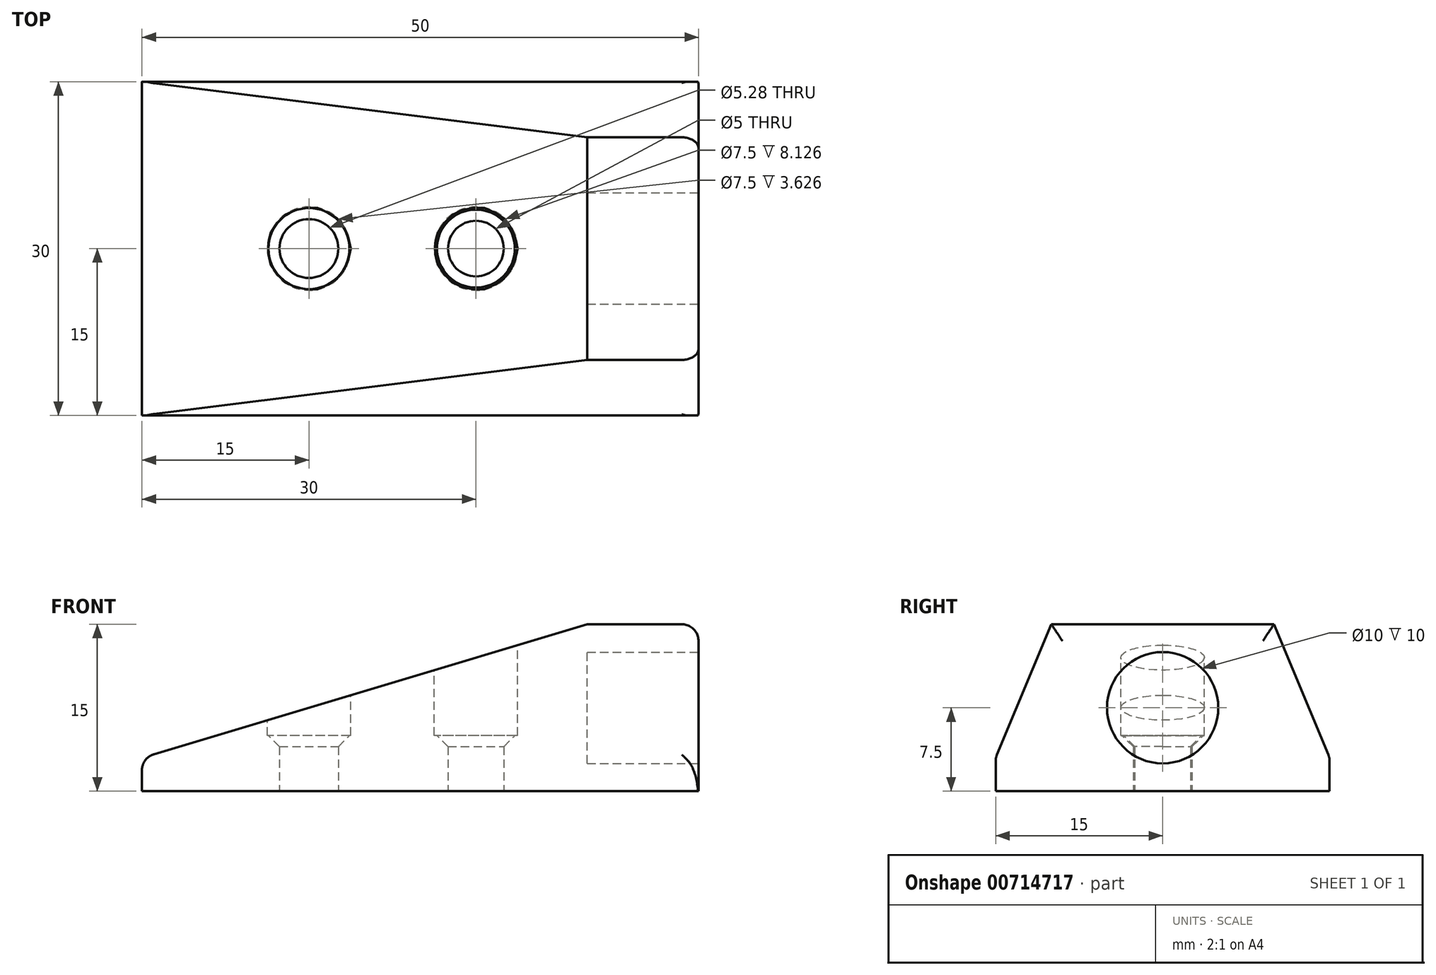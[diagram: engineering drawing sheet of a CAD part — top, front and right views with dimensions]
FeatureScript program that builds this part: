
annotation { "Feature Type Name" : "Feature", "Feature Type Description" : "" }
export const myFeature = defineFeature(function(context is Context, id is Id, definition is map)
    precondition{}
    {
        {
            var Q0;
            Q0=qCreatedBy(makeId("Top.planeOp"),FACE);
            var sketch = newSketch(context, id + "F0", { "sketchPlane" : qUnion([Q0])});
            skLineSegment(sketch, "E0.bottom", {"start": v(-40, 15) * mm, "end": v(10, 15) * mm});
            skLineSegment(sketch, "E0.top", {"start": v(-40, -15) * mm, "end": v(10, -15) * mm});
            skLineSegment(sketch, "E0.left", {"start": v(-40, 15) * mm, "end": v(-40, -15) * mm});
            skLineSegment(sketch, "E0.right", {"start": v(10, 15) * mm, "end": v(10, -15) * mm});
            skSolve(sketch);
        }
        {
            var Q0;
            Q0=makeQuery(id+"F0.imprint","IMPRINT",FACE,{"disambiguationData":[TD([[makeQuery(id+"F0.imprint","IMPRINT",EDGE,{"derivedFrom":sQuery(id+"F0.wireOp",EDGE,"E0.bottom")}),-1.0]])]});
            extrude(context, id + "F1", {"entities" : qUnion([Q0]), "depth" : 15 * mm, "offsetDistance" : 25 * mm});
        }
        {
            var Q0;
            Q0=makeQuery(id+"F1.opExtrude","CAP_EDGE",EDGE,{"disambiguationData":[OSD([sQuery(id+"F0.wireOp",EDGE,"E0.left")])],"isStart":false});
            chamfer(context, id + "F2", {"entities" : qUnion([Q0]), "chamferType" : ChamferType.TWO_OFFSETS, "width1" : 40 * mm, "oppositeDirection" : false, "width2" : 12 * mm, "tangentPropagation" : true});
        }
        {
            var Q0;
            Q0=makeQuery(id+"F1.opExtrude","CAP_EDGE",EDGE,{"disambiguationData":[OSD([sQuery(id+"F0.wireOp",EDGE,"E0.bottom")])],"isStart":false});
            chamfer(context, id + "F3", {"entities" : qUnion([Q0]), "chamferType" : ChamferType.TWO_OFFSETS, "width1" : 12 * mm, "oppositeDirection" : false, "width2" : 5 * mm, "tangentPropagation" : true});
        }
        {
            var Q0;
            Q0=makeQuery(id+"F1.opExtrude","CAP_EDGE",EDGE,{"disambiguationData":[OSD([sQuery(id+"F0.wireOp",EDGE,"E0.top")])],"isStart":false});
            chamfer(context, id + "F4", {"entities" : qUnion([Q0]), "chamferType" : ChamferType.TWO_OFFSETS, "width1" : 5 * mm, "oppositeDirection" : false, "width2" : 12 * mm, "tangentPropagation" : true});
        }
        {
            var Q0;
            {var subQ0=sQuery(id+"F0.wireOp",EDGE,"E0.left");Q0=makeQuery(id+"F2.opChamfer","BLEND_EDGE",EDGE,{"blendedFrom":[makeQuery(id+"F1.opExtrude","CAP_EDGE",EDGE,{"disambiguationData":[OSD([subQ0])],"isStart":false}),makeQuery(id+"F1.opExtrude","SWEPT_FACE",FACE,{"disambiguationData":[OSD([subQ0])]})],"blendedInto":[makeQuery(id+"F1.opExtrude","SWEPT_FACE",FACE,{"disambiguationData":[OSD([subQ0])]})]});}
            var Q1;
            {var subQ0=sQuery(id+"F0.wireOp",EDGE,"E0.top");Q1=makeQuery(id+"F4.opChamfer","BLEND_EDGE",EDGE,{"blendedFrom":[makeQuery(id+"F1.opExtrude","CAP_EDGE",EDGE,{"disambiguationData":[OSD([subQ0])],"isStart":false}),makeQuery(id+"F1.opExtrude","SWEPT_FACE",FACE,{"disambiguationData":[OSD([subQ0])]})],"blendedInto":[makeQuery(id+"F1.opExtrude","SWEPT_FACE",FACE,{"disambiguationData":[OSD([subQ0])]})]});}
            var Q2;
            {var subQ0=sQuery(id+"F0.wireOp",EDGE,"E0.bottom");Q2=makeQuery(id+"F3.opChamfer","BLEND_EDGE",EDGE,{"blendedFrom":[makeQuery(id+"F1.opExtrude","CAP_EDGE",EDGE,{"disambiguationData":[OSD([subQ0])],"isStart":false}),makeQuery(id+"F1.opExtrude","SWEPT_FACE",FACE,{"disambiguationData":[OSD([subQ0])]})],"blendedInto":[makeQuery(id+"F1.opExtrude","SWEPT_FACE",FACE,{"disambiguationData":[OSD([subQ0])]})]});}
            var Q3;
            Q3=makeQuery(id+"F4.opChamfer","BLEND_EDGE",EDGE,{"blendedFrom":[makeQuery(id+"F1.opExtrude","CAP_EDGE",EDGE,{"disambiguationData":[OSD([sQuery(id+"F0.wireOp",EDGE,"E0.top")])],"isStart":false}),makeQuery(id+"F1.opExtrude","SWEPT_FACE",FACE,{"disambiguationData":[OSD([sQuery(id+"F0.wireOp",EDGE,"E0.right")])]})],"blendedInto":[makeQuery(id+"F1.opExtrude","SWEPT_FACE",FACE,{"disambiguationData":[OSD([sQuery(id+"F0.wireOp",EDGE,"E0.right")])]})]});
            var Q4;
            Q4=makeQuery(id+"F1.opExtrude","CAP_EDGE",EDGE,{"disambiguationData":[OSD([sQuery(id+"F0.wireOp",EDGE,"E0.right")])],"isStart":false});
            var Q5;
            Q5=makeQuery(id+"F3.opChamfer","BLEND_EDGE",EDGE,{"blendedFrom":[makeQuery(id+"F1.opExtrude","CAP_EDGE",EDGE,{"disambiguationData":[OSD([sQuery(id+"F0.wireOp",EDGE,"E0.bottom")])],"isStart":false}),makeQuery(id+"F1.opExtrude","SWEPT_FACE",FACE,{"disambiguationData":[OSD([sQuery(id+"F0.wireOp",EDGE,"E0.right")])]})],"blendedInto":[makeQuery(id+"F1.opExtrude","SWEPT_FACE",FACE,{"disambiguationData":[OSD([sQuery(id+"F0.wireOp",EDGE,"E0.right")])]})]});
            fillet(context, id + "F5", {"entities" : qUnion([Q0, Q1, Q2, Q3, Q4, Q5]), "radius" : 1.5 * mm, "tangentPropagation" : true, "allowEdgeOverflow" : false});
        }
        {
            var Q0;
            Q0=makeQuery(id+"F1.opExtrude","SWEPT_FACE",FACE,{"disambiguationData":[OSD([sQuery(id+"F0.wireOp",EDGE,"E0.right")])]});
            var sketch = newSketch(context, id + "F6", { "sketchPlane" : qUnion([Q0])});
            skCircle(sketch, "E1", {"center": v(0, 7.5) * mm, "radius": 5 * mm});
            skSolve(sketch);
        }
        {
            var Q0;
            Q0=makeQuery(id+"F6.imprint","IMPRINT",FACE,{"disambiguationData":[TD([[makeQuery(id+"F6.imprint","IMPRINT",EDGE,{"derivedFrom":sQuery(id+"F6.wireOp",EDGE,"E1")}),1.0]])]});
            extrude(context, id + "F7", {"entities" : qUnion([Q0]), "operationType" : NewBodyOperationType.REMOVE, "oppositeDirection" : true, "depth" : 10 * mm, "offsetDistance" : 25 * mm});
        }
        {
            var Q0;
            Q0=makeQuery(id+"F1.opExtrude","CAP_FACE",FACE,{"disambiguationData":[OSD([sQuery(id+"F0.wireOp",EDGE,"E0.bottom"),sQuery(id+"F0.wireOp",EDGE,"E0.top"),sQuery(id+"F0.wireOp",EDGE,"E0.left"),sQuery(id+"F0.wireOp",EDGE,"E0.right")])],"isStart":true});
            var sketch = newSketch(context, id + "F8", { "sketchPlane" : qUnion([Q0])});
            skCircle(sketch, "E2", {"center": v(-25, 0) * mm, "radius": 2.64 * mm});
            skCircle(sketch, "E3", {"center": v(-10, 0) * mm, "radius": 2.5 * mm});
            skSolve(sketch);
        }
        {
            var Q0;
            Q0=makeQuery(id+"F8.imprint","IMPRINT",FACE,{"disambiguationData":[TD([[makeQuery(id+"F8.imprint","IMPRINT",EDGE,{"derivedFrom":sQuery(id+"F8.wireOp",EDGE,"E3")}),1.0]])]});
            var Q1;
            Q1=makeQuery(id+"F8.imprint","IMPRINT",FACE,{"disambiguationData":[TD([[makeQuery(id+"F8.imprint","IMPRINT",EDGE,{"derivedFrom":sQuery(id+"F8.wireOp",EDGE,"E2")}),1.0]])]});
            extrude(context, id + "F9", {"entities" : qUnion([Q0, Q1]), "operationType" : NewBodyOperationType.REMOVE, "oppositeDirection" : true, "depth" : 40 * mm, "offsetDistance" : 25 * mm});
        }
        {
            var Q0;
            Q0=makeQuery(id+"F1.opExtrude","CAP_FACE",FACE,{"disambiguationData":[OSD([sQuery(id+"F0.wireOp",EDGE,"E0.bottom"),sQuery(id+"F0.wireOp",EDGE,"E0.top"),sQuery(id+"F0.wireOp",EDGE,"E0.left"),sQuery(id+"F0.wireOp",EDGE,"E0.right")])],"isStart":false});
            var sketch = newSketch(context, id + "F10", { "sketchPlane" : qUnion([Q0])});
            skCircle(sketch, "E4", {"center": v(-10, 0) * mm, "radius": 3.75 * mm});
            skCircle(sketch, "E5", {"center": v(-25, 0) * mm, "radius": 3.75 * mm});
            skSolve(sketch);
        }
        {
            var Q0;
            Q0=makeQuery(id+"F10.imprint","IMPRINT",FACE,{"disambiguationData":[TD([[makeQuery(id+"F10.imprint","IMPRINT",EDGE,{"derivedFrom":sQuery(id+"F10.wireOp",EDGE,"E4")}),1.0]])]});
            var Q1;
            Q1=makeQuery(id+"F10.imprint","IMPRINT",FACE,{"disambiguationData":[TD([[makeQuery(id+"F10.imprint","IMPRINT",EDGE,{"derivedFrom":sQuery(id+"F10.wireOp",EDGE,"E5")}),1.0]])]});
            extrude(context, id + "F11", {"entities" : qUnion([Q0, Q1]), "operationType" : NewBodyOperationType.REMOVE, "oppositeDirection" : true, "depth" : 10 * mm, "offsetDistance" : 25 * mm});
        }
        {
            var Q0;
            Q0=makeQuery(id+"F11.boolean.opBoolean","INTERSECT",EDGE,{"derivedFrom":[makeQuery(id+"F9.boolean.opBoolean","COPY",FACE,{"derivedFrom":makeQuery(id+"F9.opExtrude","SWEPT_FACE",FACE,{"disambiguationData":[OSD([sQuery(id+"F8.wireOp",EDGE,"E2")])]})}),makeQuery(id+"F11.opExtrude","CAP_FACE",FACE,{"disambiguationData":[OSD([sQuery(id+"F10.wireOp",EDGE,"E5")])],"isStart":false})]});
            var Q1;
            Q1=makeQuery(id+"F11.boolean.opBoolean","INTERSECT",EDGE,{"derivedFrom":[makeQuery(id+"F9.boolean.opBoolean","COPY",FACE,{"derivedFrom":makeQuery(id+"F9.opExtrude","SWEPT_FACE",FACE,{"disambiguationData":[OSD([sQuery(id+"F8.wireOp",EDGE,"E3")])]})}),makeQuery(id+"F11.opExtrude","CAP_FACE",FACE,{"disambiguationData":[OSD([sQuery(id+"F10.wireOp",EDGE,"E4")])],"isStart":false})]});
            chamfer(context, id + "F12", {"entities" : qUnion([Q0, Q1]), "width" : 1 * mm, "tangentPropagation" : true});
        }
    });
